# Revit family: Doorset_Porte palière FOXEO BN_ASSA ABLOY FR_Hardware 3D
name_source: partatom
category: Portes
revit_build: Autodesk Revit 2018 (Build: 20190510_1515(x64)
units: mm (PartAtom-declared; Revit-internal decimal feet)

## family parameters
Couper avec des vides une fois chargée = Non
Hôte = Mur
Numéro OmniClass = 23.30.10.00
Partagée = Non
Point de calcul de pièce = Non
Titre OmniClass = Doors
Toujours verticalement = Oui

## types (2) — shared parameters
Clear Width = 852 mm  [stored 2.79528 ft]
Code d'assemblage = C1020
Commentaires du type = 914x2198 mm (900 x 2200mm)
Construction analytique = <Aucun>
Description = Porte palière FICHET anti-effraction classe 3 selon EN 1627-1630 2011 et EI130 contre le feu
Epaisseur = 51 mm
Fabricant = ASSA ABLOY
Fermeture du mur = Par hôte
Fonction = Intérieur
Frame Height = 2200 mm
Frame Material = Metal - Assa Abloy - Steel
Frame Width = 900 mm  [stored 2.95276 ft]
Handle Height = 1100 mm
Handle Position = 50 mm  [stored 0.164042 ft]
Hardware Set = SD-ML-MC-FI03
Hauteur = 2200 mm
Hauteur brute = 2210 mm  [stored 7.25066 ft]
IFC classification = Door
Identity and Access Solutions = 1x Serrure Fichet 3 points _Identity and Access Solutions_FICHET [AN.  98606170]
Largeur = 900 mm  [stored 2.95276 ft]
Largeur brute = 920 mm
Lock Cases = 1x Cylindre ORIO_Mechanical locks_Fichet [AN.  73100431]
Maximum Door Height = 2325 mm
Maximum Door Width = 1050 mm
Minimum Door Height = 1925 mm
Minimum Door Width = 650 mm
Modèle = Doorset_Porte palière FOXEO BN_ASSA ABLOY FR_Hardware 3D
Name = Porte palière FOXEO BN
Note d'identification = 08100
OmniClass Number = 23-17 11 00
OmniClass Title = Doors
Panel Height = 2198 mm
Panel Material = Metal - Assa Abloy - Steel
Panel Width = 914 mm
Protection contre l'incendie = EI130
Provider = ASSA ABLOY FR
Structural Opening Height = 2210 mm  [stored 7.25066 ft]
Structural Opening Width = 920 mm
URL = https://www.fichet-serrurerie-batiment.com
Uniclass 1.4 Code = JL20
Uniclass 1.4 Description = Doors
Uniclass 2.0 Code = PR-59-23
Uniclass 2.0 Description = Doorsets

## per-type parameters (varying)
| type | Architectural Hardware | Handle |
| 914x2198 mm (900 x 2200mm) - sur plaque | 1x Ensemble béquillage ARTIS sur plaque_Architectural hardware_Vachette [AN.  73490310] | Architectural Hardware_Poignée Artis palière_ASSA ABLOY FR_73490310 : Poignée Artis palière_73490310 |
| 914x2198 mm (900 x 2200mm) - sur rosace | 1x Ensemble béquillage ARTIS sur rosace_Architectural hardware_Vachette [AN. 73490420] | Architectural Hardware_Poignée Artis palière_ASSA ABLOY FR_73490420 : Poignée Artis palière_73490420 |

note: [stored X ft] marks values corroborated as IEEE doubles in the binary element streams (Revit-internal decimal feet)

## geometry (parser evidence)
native form markers: Sweep x3
no freeform markers — native parametric forms only
